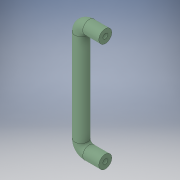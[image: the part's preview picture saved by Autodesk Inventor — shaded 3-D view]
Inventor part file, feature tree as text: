
AUTODESK INVENTOR PART (.ipt)
format: ipt  version: 2019 (Build 230136000, 136)  size: 139,776 bytes
history: native  units: mm
features: sketch x2, sweep x1
ambient origin geometry x8: Origin, YZ Plane, XZ Plane, XY Plane, X Axis, Y Axis, Z Axis, Center Point
bodies: Body1 (feature_tree)
feature tree (3):
  sweep  "Sweep2"
  sketch  "Sketch3"  dims[d4=16.0mm d5=6.0mm]
  sketch  "Sketch4"  dims[d10=0.0mm d11=0.0mm]
